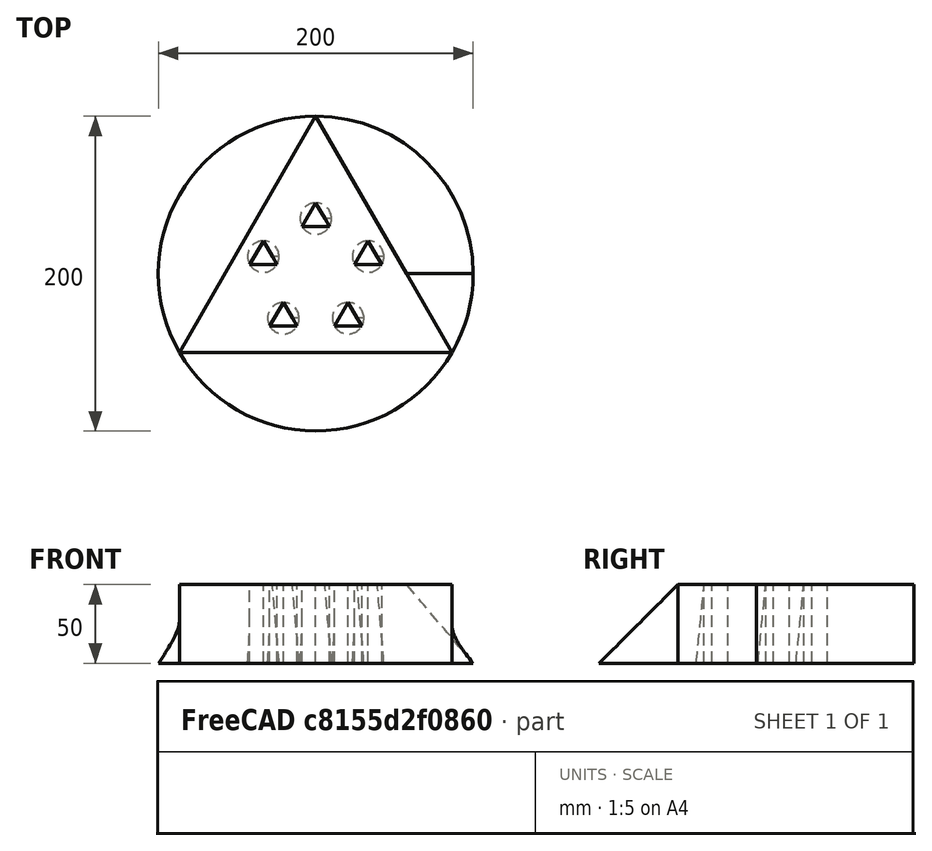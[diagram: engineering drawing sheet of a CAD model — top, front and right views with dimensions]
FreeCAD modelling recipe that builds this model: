
FCSTD DOCUMENT  (FreeCAD 0.21R32985 (Git))
Label: WireFilter_Example
License: All rights reserved
LicenseURL: http://en.wikipedia.org/wiki/All_rights_reserved
objects: Sketcher::SketchObject×2, Part::Part2DObjectPython×1, PartDesign::AdditiveLoft×1, PartDesign::Body×1
note: 6 computed .brp shape members not serialized (recipe doc carries the construction recipe); baked Part::Feature solids carry a one-line shape summary decoded from their .brp

FEATURE [Sketcher::SketchObject] Sketch
  FullyConstrained = true
  MapMode = 5
  Support = -> [XY_Plane]
  sketch-geometry (12):
    g0: Circle CenterX=0 CenterY=0 CenterZ=0 NormalX=0 NormalY=0 NormalZ=1 AngleXU=0 Radius=100
    g1: Circle CenterX=0 CenterY=35 CenterZ=0 NormalX=0 NormalY=0 NormalZ=1 AngleXU=0 Radius=10
    g2: LineSegment StartX=0 StartY=35 StartZ=0 EndX=-33.287 EndY=10.8156 EndZ=0
    g3: LineSegment StartX=-33.287 StartY=10.8156 StartZ=0 EndX=-20.5725 EndY=-28.3156 EndZ=0
    g4: LineSegment StartX=-20.5725 StartY=-28.3156 StartZ=0 EndX=20.5725 EndY=-28.3156 EndZ=0
    g5: LineSegment StartX=20.5725 StartY=-28.3156 StartZ=0 EndX=33.287 EndY=10.8156 EndZ=0
    g6: LineSegment StartX=33.287 StartY=10.8156 StartZ=0 EndX=0 EndY=35 EndZ=0
    g7: Circle CenterX=0 CenterY=0 CenterZ=0 NormalX=0 NormalY=0 NormalZ=1 AngleXU=0 Radius=35
    g8: Circle CenterX=-20.5725 CenterY=-28.3156 CenterZ=0 NormalX=0 NormalY=0 NormalZ=1 AngleXU=0 Radius=10
    g9: Circle CenterX=-33.287 CenterY=10.8156 CenterZ=0 NormalX=0 NormalY=0 NormalZ=1 AngleXU=0 Radius=10
    g10: Circle CenterX=33.287 CenterY=10.8156 CenterZ=0 NormalX=0 NormalY=0 NormalZ=1 AngleXU=0 Radius=10
    g11: Circle CenterX=20.5725 CenterY=-28.3156 CenterZ=0 NormalX=0 NormalY=0 NormalZ=1 AngleXU=0 Radius=10
  constraints (26):
    c: Coincident(g0,g-1)
    c: Coincident(g2,g3)
    c: Coincident(g3,g4)
    c: Coincident(g4,g5)
    c: Coincident(g5,g6)
    c: Coincident(g6,g2)
    c: Equal(g2, g3-g6) x4
    c: PointOnObject(g2,g7)
    c: PointOnObject(g3,g7)
    c: PointOnObject(g4,g7)
    c: PointOnObject(g5,g7)
    c: PointOnObject(g6,g7)
    c: Coincident(g7,g0)
    c: Radius(g0) = 100
    c: Radius(g1) = 10
    c: Radius(g7) = 35
    c: Horizontal(g4)
    c: Coincident(g1,g2)
    c: Coincident(g8,g3)
    c: Coincident(g9,g2)
    c: Coincident(g10,g5)
    c: Coincident(g11,g4)
    c: Equal(g9,g10)
    c: Equal(g10,g11)
    c: Equal(g11,g8)
    c: Equal(g8,g1)
FEATURE [Sketcher::SketchObject] Sketch001
  AttachmentOffset = pos=(0,0,50) rot=(0,0,1;0rad)
  ExternalGeometry = -> [Sketch]
  FullyConstrained = true
  MapMode = 5
  Placement = pos=(0,0,50) rot=(0,0,1;0rad)
  Support = -> [XY_Plane]
  sketch-geometry (24):
    g0: LineSegment StartX=-33.287 StartY=20.8156 StartZ=0 EndX=-41.9472 EndY=5.81559 EndZ=0
    g1: LineSegment StartX=-41.9472 StartY=5.81559 StartZ=0 EndX=-24.6267 EndY=5.81559 EndZ=0
    g2: LineSegment StartX=-24.6267 StartY=5.81559 StartZ=0 EndX=-33.287 EndY=20.8156 EndZ=0
    g3: Circle CenterX=-33.287 CenterY=10.8156 CenterZ=0 NormalX=0 NormalY=0 NormalZ=1 AngleXU=0 Radius=10
    g4: LineSegment StartX=-1.8e-15 StartY=45 StartZ=0 EndX=-8.66025 EndY=30 EndZ=0
    g5: LineSegment StartX=-8.66025 StartY=30 StartZ=0 EndX=8.66025 EndY=30 EndZ=0
    g6: LineSegment StartX=8.66025 StartY=30 StartZ=0 EndX=-1.8e-15 EndY=45 EndZ=0
    g7: Circle CenterX=0 CenterY=35 CenterZ=0 NormalX=0 NormalY=0 NormalZ=1 AngleXU=0 Radius=10
    g8: LineSegment StartX=20.5725 StartY=-18.3156 StartZ=0 EndX=11.9122 EndY=-33.3156 EndZ=0
    g9: LineSegment StartX=11.9122 StartY=-33.3156 StartZ=0 EndX=29.2327 EndY=-33.3156 EndZ=0
    g10: LineSegment StartX=29.2327 StartY=-33.3156 StartZ=0 EndX=20.5725 EndY=-18.3156 EndZ=0
    g11: Circle CenterX=20.5725 CenterY=-28.3156 CenterZ=0 NormalX=0 NormalY=0 NormalZ=1 AngleXU=0 Radius=10
    g12: LineSegment StartX=33.287 StartY=20.8156 StartZ=0 EndX=24.6267 EndY=5.81559 EndZ=0
    g13: LineSegment StartX=24.6267 StartY=5.81559 StartZ=0 EndX=41.9472 EndY=5.81559 EndZ=0
    g14: LineSegment StartX=41.9472 StartY=5.81559 StartZ=0 EndX=33.287 EndY=20.8156 EndZ=0
    g15: Circle CenterX=33.287 CenterY=10.8156 CenterZ=0 NormalX=0 NormalY=0 NormalZ=1 AngleXU=0 Radius=10
    g16: LineSegment StartX=-29.2327 StartY=-33.3156 StartZ=0 EndX=-11.9122 EndY=-33.3156 EndZ=0
    g17: LineSegment StartX=-11.9122 StartY=-33.3156 StartZ=0 EndX=-20.5725 EndY=-18.3156 EndZ=0
    g18: LineSegment StartX=-20.5725 StartY=-18.3156 StartZ=0 EndX=-29.2327 EndY=-33.3156 EndZ=0
    g19: Circle CenterX=-20.5725 CenterY=-28.3156 CenterZ=0 NormalX=0 NormalY=0 NormalZ=1 AngleXU=0 Radius=10
    g20: LineSegment StartX=-1.42e-14 StartY=100 StartZ=0 EndX=-86.6025 EndY=-50 EndZ=0
    g21: LineSegment StartX=-86.6025 StartY=-50 StartZ=0 EndX=86.6025 EndY=-50 EndZ=0
    g22: LineSegment StartX=86.6025 StartY=-50 StartZ=0 EndX=-1.42e-14 EndY=100 EndZ=0
    g23: Circle CenterX=0 CenterY=0 CenterZ=0 NormalX=0 NormalY=0 NormalZ=1 AngleXU=0 Radius=100
  constraints (66):
    c: Coincident(g0,g1)
    c: Coincident(g1,g2)
    c: Coincident(g2,g0)
    c: Equal(g0,g1)
    c: Equal(g0,g2)
    c: PointOnObject(g0,g3)
    c: PointOnObject(g1,g3)
    c: PointOnObject(g2,g3)
    c: Coincident(g3,g-7)
    c: Coincident(g4,g5)
    c: Coincident(g5,g6)
    c: Coincident(g6,g4)
    c: Equal(g4,g5)
    c: Equal(g4,g6)
    c: PointOnObject(g4,g7)
    c: PointOnObject(g5,g7)
    c: PointOnObject(g6,g7)
    c: Coincident(g7,g-3)
    c: Coincident(g8,g9)
    c: Coincident(g9,g10)
    c: Coincident(g10,g8)
    c: Equal(g8,g9)
    c: Equal(g8,g10)
    c: PointOnObject(g8,g11)
    c: PointOnObject(g9,g11)
    c: PointOnObject(g10,g11)
    c: Coincident(g11,g-5)
    c: Coincident(g12,g13)
    c: Coincident(g13,g14)
    c: Coincident(g14,g12)
    c: Equal(g12,g13)
    c: Equal(g12,g14)
    c: PointOnObject(g12,g15)
    c: PointOnObject(g13,g15)
    c: PointOnObject(g14,g15)
    c: Coincident(g15,g-4)
    c: Coincident(g16,g17)
    c: Coincident(g17,g18)
    c: Coincident(g18,g16)
    c: Equal(g16,g17)
    c: Equal(g16,g18)
    c: PointOnObject(g16,g19)
    c: PointOnObject(g17,g19)
    c: PointOnObject(g18,g19)
    c: Coincident(g19,g-6)
    c: Coincident(g20,g21)
    c: Coincident(g21,g22)
    c: Coincident(g22,g20)
    c: Equal(g20,g21)
    c: Equal(g20,g22)
    c: PointOnObject(g20,g23)
    c: PointOnObject(g21,g23)
    c: PointOnObject(g22,g23)
    c: Coincident(g23,g-1)
    c: Equal(g3,g-7)
    c: Equal(g-7,g7)
    c: Equal(g7,g15)
    c: Equal(g15,g11)
    c: Equal(g11,g19)
    c: Equal(g23,g-8)
    c: Horizontal(g21)
    c: Horizontal(g1)
    c: Horizontal(g5)
    c: Horizontal(g13)
    c: Horizontal(g9)
    c: Horizontal(g16)
FEATURE [Part::Part2DObjectPython] WireFilter  # Draft 2D object (typed FeaturePython)
  AttacherType = Attacher::AttachEngine3D
  ClaimChildren = true
  Colorize = true
  CompareObject = -> Sketch001
  EditWireOrder = false
  FaceMaker = 0
  FixNormal = false
  FollowSource = true
  HideGhost = false
  InvertedFaceScale = 5
  MaxWires = 25
  Normal = (0,0,1)
  OffsetFill = false
  OffsetIntersection = false
  OffsetJoin = 0
  OffsetOpenResult = false
  ReUseGhost = false
  Scale = (1,1,1)
  Source = -> Sketch
  UniformScale = 1
  UseDefault = false
  Version = 0.2023.09.08b
  WireOrder = [4,2,6,5,3,1]
FEATURE [PartDesign::AdditiveLoft] AdditiveLoft
  Closed = false
  Profile = -> WireFilter
  Ruled = false
  Sections = -> [Sketch001]
FEATURE [PartDesign::Body] Body
  Group = -> [Sketch,Sketch001,WireFilter,AdditiveLoft]
  Origin = -> Origin
  Tip = -> AdditiveLoft
